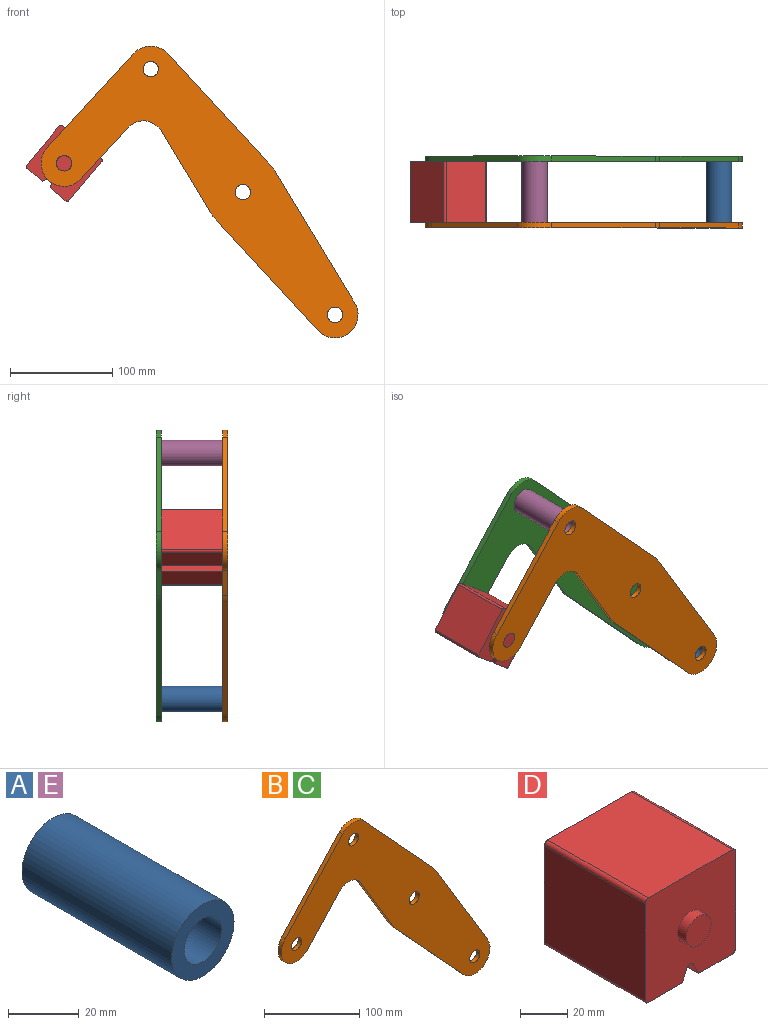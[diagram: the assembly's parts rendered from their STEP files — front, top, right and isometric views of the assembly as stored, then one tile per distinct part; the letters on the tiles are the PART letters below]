
ASSEMBLY  parts=5 mates=3
PART A: 4 faces, bbox 25x60x25 mm
  f0: cylinder r=7.5mm len=60mm, axis (0,-1,0), area 2827.4mm2, adj f2,f3
  f1: cylinder r=12.5mm len=60mm, axis (0,-1,0), area 4712.4mm2, adj f2,f3
  f2: plane 25x25mm, normal (0,-1,0), area 314.2mm2, adj f0,f1
  f3: plane 25x25mm, normal (0,1,0), area 314.2mm2, adj f0,f1
PART B: 18 faces, bbox 309.5x5x285.1 mm
  f0: cylinder r=22.5mm len=39.07mm, axis (0,1,0), area 353.4mm2, adj f1,f13,f16,f17
  f1: plane 50.28x46.21mm, normal (0.74,0,-0.68), area 341.4mm2, adj f0,f2,f16,f17
  f2: cylinder r=20mm len=31.85mm, axis (0,1,0), area 185.5mm2, adj f1,f3,f16,f17
  f3: plane 79.23x47.81mm, normal (-0.86,0,-0.52), area 462.7mm2, adj f2,f4,f16,f17
  f4: cylinder r=37.5mm len=6mm, axis (0,1,0), area 37.6mm2, adj f3,f5,f16,f17
  f5: plane 109.88x101mm, normal (-0.74,0,-0.68), area 746.2mm2, adj f4,f6,f16,f17
  f6: cylinder r=22.5mm len=39.07mm, axis (0,1,0), area 330.9mm2, adj f5,f7,f16,f17
  f7: plane 127.78x77.11mm, normal (0.86,0,0.52), area 746.2mm2, adj f6,f8,f16,f17
  f8: cylinder r=37.5mm len=6mm, axis (0,1,0), area 37.6mm2, adj f7,f9,f16,f17
  f9: plane 109.88x101mm, normal (0.74,0,0.68), area 746.2mm2, adj f8,f10,f16,f17
  f10: cylinder r=22.5mm len=33.13mm, axis (0,1,0), area 186.2mm2, adj f9,f13,f16,f17
  f11: cylinder r=7.5mm len=15mm, axis (0,1,0), area 235.6mm2, adj f16,f17
  f12: cylinder r=7.5mm len=15mm, axis (0,1,0), area 235.6mm2, adj f16,f17
  f13: plane 92.03x84.59mm, normal (-0.74,0,0.68), area 625mm2, adj f0,f10,f16,f17
  f14: cylinder r=7.5mm len=15mm, axis (0,1,0), area 235.6mm2, adj f16,f17
  f15: cylinder r=7.5mm len=15mm, axis (0,1,0), area 235.6mm2, adj f16,f17
  f16: plane 309.5x285.07mm, normal (0,-1,0), area 24555.4mm2, adj f0,f1,f2,f3,f4,f5,f6,f7
  f17: plane 309.5x285.07mm, normal (0,1,0), area 24555.4mm2, adj f0,f1,f2,f3,f4,f5,f6,f7
PART C: same geometry as B
PART D: 18 faces, bbox 54x70x54 mm
  f0: plane 60x50.01mm, normal (0,0,1), area 3000.4mm2, adj f4,f10,f13,f14
  f1: plane 60x50.01mm, normal (-1,0,0), area 3000.4mm2, adj f4,f10,f14,f15
  f2: plane 60x20mm, normal (0,0,-1), area 1200.2mm2, adj f3,f4,f10,f15
  f3: plane 60x6.42mm, normal (0.89,0,-0.45), area 430.8mm2, adj f2,f4,f10,f16
  f4: plane 54.01x54.01mm, normal (0,-1,0), area 2690.1mm2, adj f0,f1,f2,f3,f5,f6,f7,f9
  f5: plane 60x50.01mm, normal (1,0,0), area 3000.4mm2, adj f4,f10,f13,f17
  f6: plane 60x6.42mm, normal (-0.89,0,-0.45), area 430.8mm2, adj f4,f7,f10,f16
  f7: plane 60x20mm, normal (0,0,-1), area 1200.2mm2, adj f4,f6,f10,f17
  f8: plane 15x15mm, normal (0,-1,0), area 176.7mm2, adj f9
  f9: cylinder r=7.5mm len=15mm, axis (0,1,0), area 235.6mm2, adj f4,f8
  f10: plane 54.01x54.01mm, normal (0,1,0), area 2690.1mm2, adj f0,f1,f2,f3,f5,f6,f7,f12
  f11: plane 15x15mm, normal (0,1,0), area 176.7mm2, adj f12
  f12: cylinder r=7.5mm len=15mm, axis (0,-1,0), area 235.6mm2, adj f10,f11
  f13: cylinder r=2mm len=60mm, axis (0,-1,0), area 188.5mm2, adj f0,f4,f5,f10
  f14: cylinder r=2mm len=60mm, axis (0,1,0), area 188.5mm2, adj f0,f1,f4,f10
  f15: cylinder r=2mm len=60mm, axis (0,-1,0), area 188.5mm2, adj f1,f2,f4,f10
  f16: cylinder r=2mm len=60mm, axis (0,-1,0), area 265.7mm2, adj f3,f4,f6,f10
  f17: cylinder r=2mm len=60mm, axis (0,1,0), area 188.5mm2, adj f4,f5,f7,f10
PART E: same geometry as A
PLACE A t=(179.91,-30,-240.07)mm
PLACE B t=(0,-30,0)mm
PLACE C t=(0,35,0)mm
PLACE D rot(axis=(0,1,0),39.9deg) t=(-58.62,-30,-105.46)mm
PLACE E t=(0,-30,0)mm fixed
MATE fastened B.f6 <-> A.f0  axis (0,1,0) through (89.96,-30,-120.03)mm
MATE fastened E.f0 <-> C.f10  axis (0,1,0) through (-89.96,30,120.03)mm
MATE revolute B.f0 <-> D.f9  axis (0,1,0) through (-174.54,-30,28)mm
